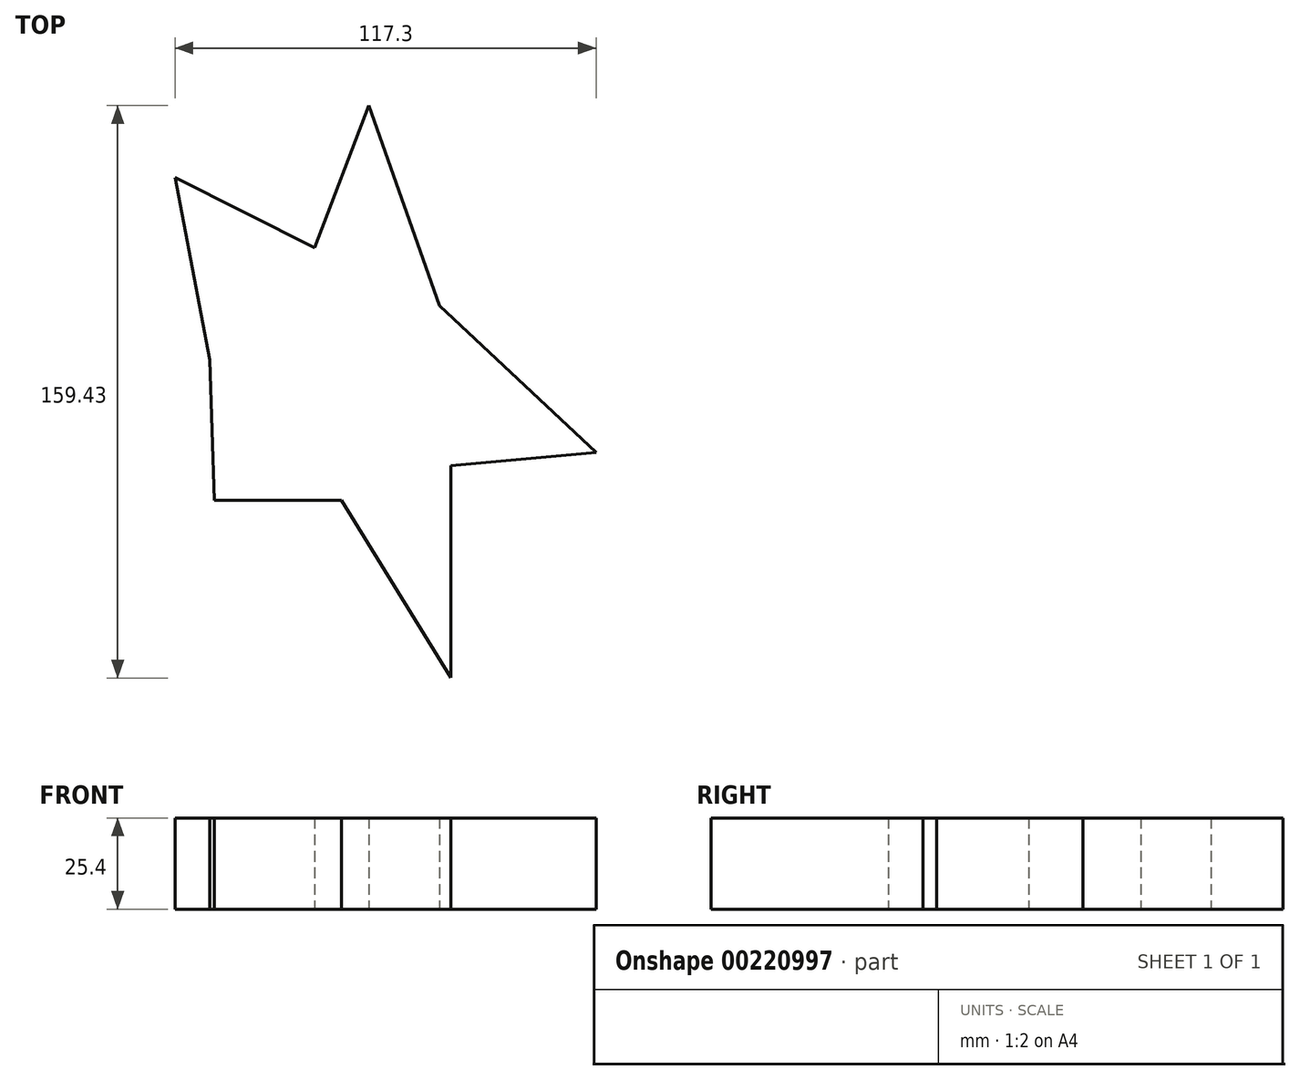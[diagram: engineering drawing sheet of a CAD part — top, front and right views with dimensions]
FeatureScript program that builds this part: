
annotation { "Feature Type Name" : "Feature", "Feature Type Description" : "" }
export const myFeature = defineFeature(function(context is Context, id is Id, definition is map)
    precondition{}
    {
        {
            var Q0;
            Q0=qCreatedBy(makeId("Top.planeOp"),FACE);
            var sketch = newSketch(context, id + "F0", { "sketchPlane" : qUnion([Q0])});
            skLineSegment(sketch, "E0", {"start": v(-25.68, -15.15) * mm, "end": v(-35.34, 35.66) * mm});
            skLineSegment(sketch, "E1", {"start": v(-35.34, 35.66) * mm, "end": v(3.49, 16.11) * mm});
            skLineSegment(sketch, "E2", {"start": v(3.49, 16.11) * mm, "end": v(18.66, 55.7) * mm});
            skLineSegment(sketch, "E3", {"start": v(18.66, 55.7) * mm, "end": v(38.28, 0) * mm});
            skLineSegment(sketch, "E4", {"start": v(38.28, 0) * mm, "end": v(81.96, -40.88) * mm});
            skLineSegment(sketch, "E5", {"start": v(81.96, -40.88) * mm, "end": v(41.47, -44.58) * mm});
            skLineSegment(sketch, "E6", {"start": v(41.47, -44.58) * mm, "end": v(41.47, -103.74) * mm});
            skLineSegment(sketch, "E7", {"start": v(41.47, -103.74) * mm, "end": v(11.02, -54.3) * mm});
            skLineSegment(sketch, "E8", {"start": v(11.02, -54.3) * mm, "end": v(-24.4, -54.3) * mm});
            skLineSegment(sketch, "E9", {"start": v(-24.4, -54.3) * mm, "end": v(-25.68, -15.15) * mm});
            skSolve(sketch);
        }
        {
            var Q0;
            Q0 = qSketchRegion(id + "F0", true);
            extrude(context, id + "F1", {"entities" : qUnion([Q0]), "depth" : 25.4 * mm});
        }
    });
